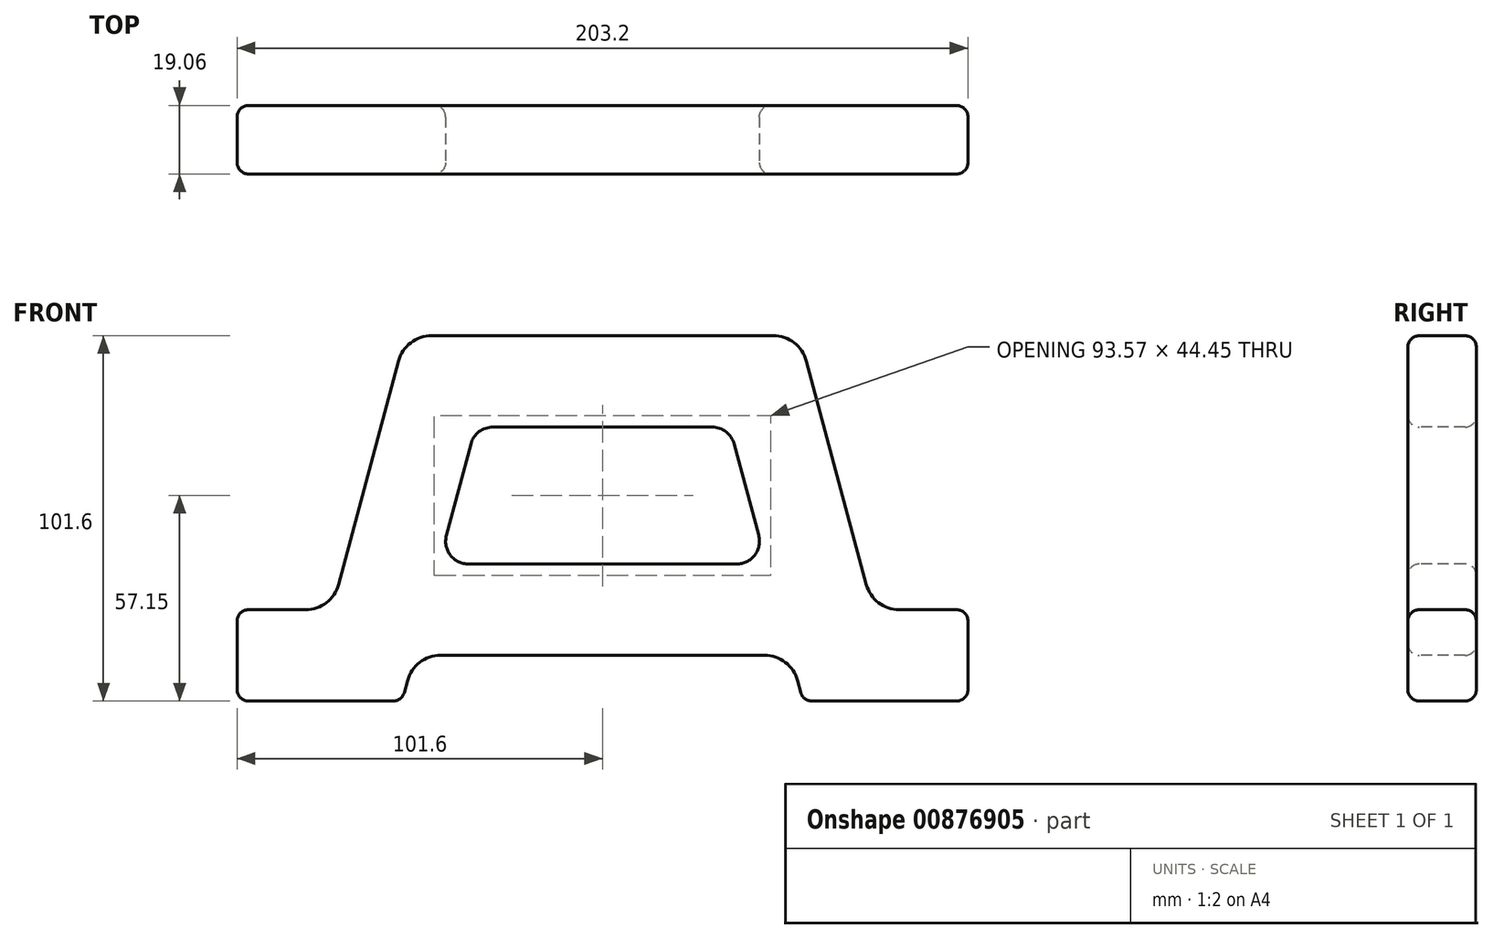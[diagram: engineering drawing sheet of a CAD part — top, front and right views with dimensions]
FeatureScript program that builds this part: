
annotation { "Feature Type Name" : "Feature", "Feature Type Description" : "" }
export const myFeature = defineFeature(function(context is Context, id is Id, definition is map)
    precondition{}
    {
        {
            var Q0;
            Q0=qCreatedBy(makeId("Front.planeOp"),FACE);
            var sketch = newSketch(context, id + "F0", { "sketchPlane" : qUnion([Q0])});
            skLineSegment(sketch, "E0", {"start": v(-56.72, 81.84) * mm, "end": v(-73.35, 19.76) * mm});
            skLineSegment(sketch, "E1", {"start": v(-82.55, 12.7) * mm, "end": v(-98.43, 12.7) * mm});
            skLineSegment(sketch, "E2", {"start": v(-101.6, 9.52) * mm, "end": v(-101.6, -9.53) * mm});
            skLineSegment(sketch, "E3", {"start": v(-98.43, -12.7) * mm, "end": v(-58.19, -12.7) * mm});
            skLineSegment(sketch, "E4", {"start": v(-55.12, -10.35) * mm, "end": v(-54.24, -7.06) * mm});
            skLineSegment(sketch, "E5", {"start": v(-45.04, 0) * mm, "end": v(45.04, 0) * mm});
            skLineSegment(sketch, "E6", {"start": v(54.24, -7.06) * mm, "end": v(55.12, -10.35) * mm});
            skLineSegment(sketch, "E7", {"start": v(58.19, -12.7) * mm, "end": v(98.43, -12.7) * mm});
            skLineSegment(sketch, "E8", {"start": v(101.6, -9.53) * mm, "end": v(101.6, 9.52) * mm});
            skLineSegment(sketch, "E9", {"start": v(98.43, 12.7) * mm, "end": v(82.55, 12.7) * mm});
            skLineSegment(sketch, "E10", {"start": v(73.35, 19.76) * mm, "end": v(56.72, 81.84) * mm});
            skLineSegment(sketch, "E11", {"start": v(47.51, 88.9) * mm, "end": v(-47.51, 88.9) * mm});
            skLineSegment(sketch, "E12", {"start": v(-36.6, 58.8) * mm, "end": v(-43.4, 33.4) * mm});
            skLineSegment(sketch, "E13", {"start": v(-37.27, 25.4) * mm, "end": v(37.27, 25.4) * mm});
            skLineSegment(sketch, "E14", {"start": v(43.4, 33.4) * mm, "end": v(36.6, 58.8) * mm});
            skLineSegment(sketch, "E15", {"start": v(30.46, 63.5) * mm, "end": v(-30.46, 63.5) * mm});
            skLineSegment(sketch, "E16", {"start": v(0, 0) * mm, "end": v(0, 88.9) * mm, "construction": true});
            skPoint(sketch, "E17.visualSharp", {"position": v(-55.75, -12.7) * mm});
            skArc(sketch, "E18.filletArc", {"start": v(-45.04, 0) * mm, "mid": v(-50.84, -1.97) * mm, "end": v(-54.24, -7.06) * mm});
            skArc(sketch, "E19.filletArc", {"start": v(54.24, -7.06) * mm, "mid": v(50.84, -1.97) * mm, "end": v(45.04, 0) * mm});
            skPoint(sketch, "E20.visualSharp", {"position": v(55.75, -12.7) * mm});
            skArc(sketch, "E20.filletArc", {"start": v(55.12, -10.35) * mm, "mid": v(56.25, -12.04) * mm, "end": v(58.19, -12.7) * mm});
            skPoint(sketch, "E21.visualSharp", {"position": v(101.6, -12.7) * mm});
            skArc(sketch, "E21.filletArc", {"start": v(98.43, -12.7) * mm, "mid": v(100.67, -11.77) * mm, "end": v(101.6, -9.52) * mm});
            skPoint(sketch, "E22.visualSharp", {"position": v(101.6, 12.7) * mm});
            skArc(sketch, "E22.filletArc", {"start": v(101.6, 9.53) * mm, "mid": v(100.67, 11.77) * mm, "end": v(98.43, 12.7) * mm});
            skPoint(sketch, "E23.visualSharp", {"position": v(75.24, 12.7) * mm});
            skArc(sketch, "E23.filletArc", {"start": v(73.35, 19.76) * mm, "mid": v(76.75, 14.67) * mm, "end": v(82.55, 12.7) * mm});
            skPoint(sketch, "E24.visualSharp", {"position": v(45.54, 25.4) * mm});
            skArc(sketch, "E24.filletArc", {"start": v(37.27, 25.4) * mm, "mid": v(42.3, 27.88) * mm, "end": v(43.4, 33.4) * mm});
            skPoint(sketch, "E25.visualSharp", {"position": v(35.33, 63.5) * mm});
            skArc(sketch, "E25.filletArc", {"start": v(36.6, 58.8) * mm, "mid": v(34.33, 62.19) * mm, "end": v(30.46, 63.5) * mm});
            skPoint(sketch, "E26.visualSharp", {"position": v(-35.33, 63.5) * mm});
            skArc(sketch, "E26.filletArc", {"start": v(-30.46, 63.5) * mm, "mid": v(-34.33, 62.19) * mm, "end": v(-36.6, 58.8) * mm});
            skPoint(sketch, "E27.visualSharp", {"position": v(-45.54, 25.4) * mm});
            skArc(sketch, "E27.filletArc", {"start": v(-43.4, 33.4) * mm, "mid": v(-42.3, 27.88) * mm, "end": v(-37.27, 25.4) * mm});
            skPoint(sketch, "E28.visualSharp", {"position": v(-54.82, 88.9) * mm});
            skArc(sketch, "E28.filletArc", {"start": v(-47.51, 88.9) * mm, "mid": v(-53.31, 86.93) * mm, "end": v(-56.72, 81.84) * mm});
            skPoint(sketch, "E29.visualSharp", {"position": v(54.82, 88.9) * mm});
            skArc(sketch, "E29.filletArc", {"start": v(56.72, 81.84) * mm, "mid": v(53.31, 86.93) * mm, "end": v(47.51, 88.9) * mm});
            skPoint(sketch, "E30.visualSharp", {"position": v(-75.24, 12.7) * mm});
            skArc(sketch, "E30.filletArc", {"start": v(-82.55, 12.7) * mm, "mid": v(-76.75, 14.67) * mm, "end": v(-73.35, 19.76) * mm});
            skPoint(sketch, "E31.visualSharp", {"position": v(-101.6, 12.7) * mm});
            skArc(sketch, "E31.filletArc", {"start": v(-98.43, 12.7) * mm, "mid": v(-100.67, 11.77) * mm, "end": v(-101.6, 9.52) * mm});
            skPoint(sketch, "E32.visualSharp", {"position": v(-101.6, -12.7) * mm});
            skArc(sketch, "E32.filletArc", {"start": v(-101.6, -9.53) * mm, "mid": v(-100.67, -11.77) * mm, "end": v(-98.43, -12.7) * mm});
            skArc(sketch, "E33", {"start": v(-58.19, -12.7) * mm, "mid": v(-56.25, -12.04) * mm, "end": v(-55.12, -10.35) * mm});
            skSolve(sketch);
        }
        {
            var Q0;
            Q0=makeQuery(id+"F0.imprint","IMPRINT",FACE,{"disambiguationData":[TD([[makeQuery(id+"F0.imprint","IMPRINT",EDGE,{"derivedFrom":sQuery(id+"F0.wireOp",EDGE,"E0")}),1.0]])]});
            extrude(context, id + "F1", {"entities" : qUnion([Q0]), "endBound" : BoundingType.SYMMETRIC, "oppositeDirection" : true, "depth" : 19.05 * mm, "offsetDistance" : 25.4 * mm});
        }
        {
            var Q0;
            Q0=makeQuery(id+"F1.opExtrude","CAP_FACE",FACE,{"disambiguationData":[OSD([sQuery(id+"F0.wireOp",EDGE,"E0"),sQuery(id+"F0.wireOp",EDGE,"E1"),sQuery(id+"F0.wireOp",EDGE,"E2"),sQuery(id+"F0.wireOp",EDGE,"E3"),sQuery(id+"F0.wireOp",EDGE,"E4"),sQuery(id+"F0.wireOp",EDGE,"E5"),sQuery(id+"F0.wireOp",EDGE,"E6"),sQuery(id+"F0.wireOp",EDGE,"E7"),sQuery(id+"F0.wireOp",EDGE,"E8"),sQuery(id+"F0.wireOp",EDGE,"E9"),sQuery(id+"F0.wireOp",EDGE,"E10"),sQuery(id+"F0.wireOp",EDGE,"E11"),sQuery(id+"F0.wireOp",EDGE,"E12"),sQuery(id+"F0.wireOp",EDGE,"E13"),sQuery(id+"F0.wireOp",EDGE,"E14"),sQuery(id+"F0.wireOp",EDGE,"E15"),sQuery(id+"F0.wireOp",EDGE,"E18.filletArc"),sQuery(id+"F0.wireOp",EDGE,"E19.filletArc"),sQuery(id+"F0.wireOp",EDGE,"E20.filletArc"),sQuery(id+"F0.wireOp",EDGE,"E21.filletArc"),sQuery(id+"F0.wireOp",EDGE,"E22.filletArc"),sQuery(id+"F0.wireOp",EDGE,"E23.filletArc"),sQuery(id+"F0.wireOp",EDGE,"E24.filletArc"),sQuery(id+"F0.wireOp",EDGE,"E25.filletArc"),sQuery(id+"F0.wireOp",EDGE,"E26.filletArc"),sQuery(id+"F0.wireOp",EDGE,"E27.filletArc"),sQuery(id+"F0.wireOp",EDGE,"E28.filletArc"),sQuery(id+"F0.wireOp",EDGE,"E29.filletArc"),sQuery(id+"F0.wireOp",EDGE,"E30.filletArc"),sQuery(id+"F0.wireOp",EDGE,"E31.filletArc"),sQuery(id+"F0.wireOp",EDGE,"E32.filletArc"),sQuery(id+"F0.wireOp",EDGE,"E33")])],"isStart":true});
            var Q1;
            Q1=makeQuery(id+"F1.opExtrude","CAP_FACE",FACE,{"disambiguationData":[OSD([sQuery(id+"F0.wireOp",EDGE,"E0"),sQuery(id+"F0.wireOp",EDGE,"E1"),sQuery(id+"F0.wireOp",EDGE,"E2"),sQuery(id+"F0.wireOp",EDGE,"E3"),sQuery(id+"F0.wireOp",EDGE,"E4"),sQuery(id+"F0.wireOp",EDGE,"E5"),sQuery(id+"F0.wireOp",EDGE,"E6"),sQuery(id+"F0.wireOp",EDGE,"E7"),sQuery(id+"F0.wireOp",EDGE,"E8"),sQuery(id+"F0.wireOp",EDGE,"E9"),sQuery(id+"F0.wireOp",EDGE,"E10"),sQuery(id+"F0.wireOp",EDGE,"E11"),sQuery(id+"F0.wireOp",EDGE,"E12"),sQuery(id+"F0.wireOp",EDGE,"E13"),sQuery(id+"F0.wireOp",EDGE,"E14"),sQuery(id+"F0.wireOp",EDGE,"E15"),sQuery(id+"F0.wireOp",EDGE,"E18.filletArc"),sQuery(id+"F0.wireOp",EDGE,"E19.filletArc"),sQuery(id+"F0.wireOp",EDGE,"E20.filletArc"),sQuery(id+"F0.wireOp",EDGE,"E21.filletArc"),sQuery(id+"F0.wireOp",EDGE,"E22.filletArc"),sQuery(id+"F0.wireOp",EDGE,"E23.filletArc"),sQuery(id+"F0.wireOp",EDGE,"E24.filletArc"),sQuery(id+"F0.wireOp",EDGE,"E25.filletArc"),sQuery(id+"F0.wireOp",EDGE,"E26.filletArc"),sQuery(id+"F0.wireOp",EDGE,"E27.filletArc"),sQuery(id+"F0.wireOp",EDGE,"E28.filletArc"),sQuery(id+"F0.wireOp",EDGE,"E29.filletArc"),sQuery(id+"F0.wireOp",EDGE,"E30.filletArc"),sQuery(id+"F0.wireOp",EDGE,"E31.filletArc"),sQuery(id+"F0.wireOp",EDGE,"E32.filletArc"),sQuery(id+"F0.wireOp",EDGE,"E33")])],"isStart":false});
            fillet(context, id + "F2", {"entities" : qUnion([Q0, Q1]), "radius" : 3.17 * mm, "tangentPropagation" : true, "allowEdgeOverflow" : false});
        }
    });
